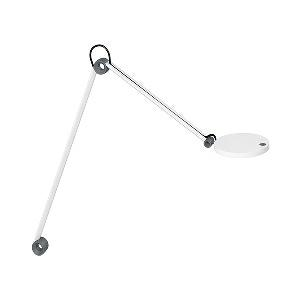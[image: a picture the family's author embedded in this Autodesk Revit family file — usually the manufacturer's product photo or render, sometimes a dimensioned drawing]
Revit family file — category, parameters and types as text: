
# Revit family: para_mi_-_ftl_102_r__940_00638507_5d64
name_source: partatom
category: Lighting Fixtures
units: mm (PartAtom-declared; Revit-internal decimal feet)

## family parameters
Cut with Voids When Loaded = No
Host = Face
Light Source = No
Part Type = Normal
Room Calculation Point = No
Round Connector Dimension = Use Diameter
Shared = No

## types (1)
- PARA.MI - FTL 102 R /940 (1 x LED, 600 lm, 4000K)
    Apparent Load = 7 VA
    Approval mark = CE
    CIE Flux Codes = 69 94 99 100 100
    Color Rendering = 90-100
    Color Temperature = 4000K
    Control Gear = Electronic ballast
    Default Elevation = 1800 mm
    Description = FTL 102 R|Task luminaire|light source: LED|work equipment: Electronic plug-in transformer|connected load: 100-240 V, 50/60 Hz|Power consumption: approx. 7 W|luminous flux: 600 lm|luminous efficacy: 85 lm/W|Illuminance efficiency factor: 111 lx/W|colour temperature: Cold white, ca. 4000 K|color rendering index (CRI): >= 90|chromaticity tolerance:  3 SDCM|class of protection: II with plug-in power supply, III without plug-in power supply|technology: Continuously dimmable|luminaire body|material: Aluminium|surface: Painted|colour: White|lamp cover: Plastic, Clear|tubular sections|material: Tubular aluminium section|surface: Painted|colour: White|weight (net): approx. 1.0 kg|mains lead: 3.00 m Mains plug BS 1363, CEE 7/XVI, NEMA 1-15P|Fastening: Adaptor (accessory), Table base (accessory), Table clamp (accessory), Tap16|glare control: Reflector|special features: Automatic switchoff adjustable, Push button in luminaire head, Behaviour at net recovery adjustable|Approval mark: C - ETL - US (F. CAN U. USA), VDE - ENEC SEP LIGHT & POWER SUPPLY UNIT|
    Height = 12 mm  [stored 0.0393701 ft]
    Lamp = 1 x LED
    Lamp Light Flux = 600 lm
    Lamp count = 1
    Length = 123 mm
    Luminous efficacy = 86 lm/W
    Manufacturer = Waldmann
    ModVariant = No
    Model = 00638507
    Mounting Place = Table
    Mounting Type = Surface mounted
    Number of Poles = 1
    OnlyDefault = Yes
    Power Factor = 1
    Product Name = PARA.MI - FTL 102 R /940
    Product group = Task luminaire (office)
    ProductGroupID = 21
    Protection Class = Protection class II
    Protection Degree = IP 40
    RLX_Detail_Level = 1
    RLX_Emergency_Light_Flux = 0 lm
    RLX_Emergency_Type = 0
    RLX_Emergency_Type_DB = No
    RlxData = <blob elided: 73593 chars, md5=b6f2f2c0>
    Socket = socket
    Standby Power = 0 W
    System Light Flux = 600 lm
    System Power = 7 W
    Type Comments = Product without accessories
    Type Image = 113147000-00638507.jpg
    URL = http://relux.com
    VarID = ---
    Voltage = 230 V
    Voltage Range = 220-240 V
    Weight = 0.00 kg
    Width = 0 mm  [stored 0 ft]

note: [stored X ft] marks values corroborated as IEEE doubles in the binary element streams (Revit-internal decimal feet)

## geometry (parser evidence)
native form markers: Blend x4, Sweep x15
no freeform markers — native parametric forms only
